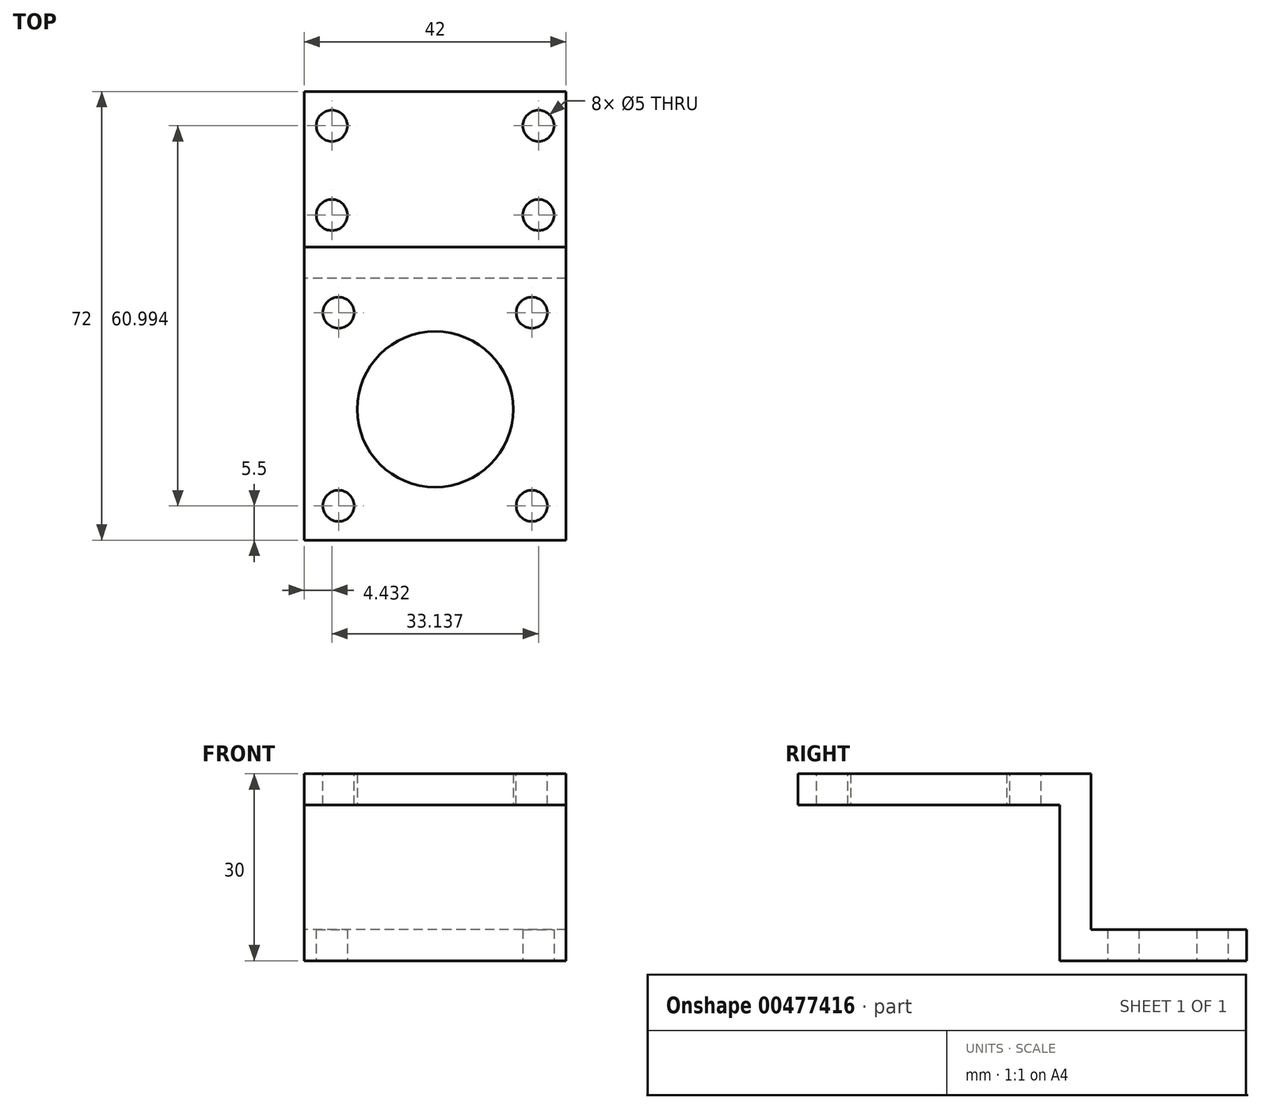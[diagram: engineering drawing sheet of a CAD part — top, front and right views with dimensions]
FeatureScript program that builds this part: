
annotation { "Feature Type Name" : "Feature", "Feature Type Description" : "" }
export const myFeature = defineFeature(function(context is Context, id is Id, definition is map)
    precondition{}
    {
        {
            var Q0;
            Q0=qCreatedBy(makeId("Top.planeOp"),FACE);
            var sketch = newSketch(context, id + "F0", { "sketchPlane" : qUnion([Q0])});
            skLineSegment(sketch, "E0.bottom", {"start": v(21, -21) * mm, "end": v(-21, -21) * mm});
            skLineSegment(sketch, "E0.top", {"start": v(21, 21) * mm, "end": v(-21, 21) * mm});
            skLineSegment(sketch, "E0.left", {"start": v(21, -21) * mm, "end": v(21, 21) * mm});
            skLineSegment(sketch, "E0.right", {"start": v(-21, -21) * mm, "end": v(-21, 21) * mm});
            skPoint(sketch, "E0.middle", {"position": v(0, 0) * mm});
            skSolve(sketch);
        }
        {
            var Q0;
            Q0=makeQuery(id+"F0.imprint","IMPRINT",FACE,{"disambiguationData":[TD([[makeQuery(id+"F0.imprint","IMPRINT",EDGE,{"derivedFrom":sQuery(id+"F0.wireOp",EDGE,"E0.bottom")}),-1.0]])]});
            extrude(context, id + "F1", {"entities" : qUnion([Q0]), "depth" : 5 * mm});
        }
        {
            var Q0;
            Q0=makeQuery(id+"F1.opExtrude","CAP_FACE",FACE,{"disambiguationData":[OSD([sQuery(id+"F0.wireOp",EDGE,"E0.bottom"),sQuery(id+"F0.wireOp",EDGE,"E0.top"),sQuery(id+"F0.wireOp",EDGE,"E0.left"),sQuery(id+"F0.wireOp",EDGE,"E0.right")])],"isStart":false});
            var sketch = newSketch(context, id + "F2", { "sketchPlane" : qUnion([Q0])});
            skLineSegment(sketch, "E1.bottom", {"start": v(15.5, -15.5) * mm, "end": v(-15.5, -15.5) * mm});
            skLineSegment(sketch, "E1.top", {"start": v(15.5, 15.5) * mm, "end": v(-15.5, 15.5) * mm});
            skLineSegment(sketch, "E1.left", {"start": v(15.5, -15.5) * mm, "end": v(15.5, 15.5) * mm});
            skLineSegment(sketch, "E1.right", {"start": v(-15.5, -15.5) * mm, "end": v(-15.5, 15.5) * mm});
            skPoint(sketch, "E1.middle", {"position": v(0, 0) * mm});
            skSolve(sketch);
        }
        {
            var Q0;
            Q0=sQuery(id+"F2.wireOp",VERTEX,"E1.top.end");
            var Q1;
            Q1=sQuery(id+"F2.wireOp",VERTEX,"E1.left.end");
            var Q2;
            Q2=sQuery(id+"F2.wireOp",VERTEX,"E1.left.start");
            var Q3;
            Q3=sQuery(id+"F2.wireOp",VERTEX,"E1.right.start");
            var Q4;
            Q4=makeQuery(id+"F1.opExtrude","SWEPT_BODY",BODY,{"disambiguationData":[OSD([sQuery(id+"F0.wireOp",EDGE,"E0.bottom"),sQuery(id+"F0.wireOp",EDGE,"E0.top"),sQuery(id+"F0.wireOp",EDGE,"E0.left"),sQuery(id+"F0.wireOp",EDGE,"E0.right")])]});
            hole(context, id + "F3", {"style" : HoleStyle.SIMPLE, "endStyle" : HoleEndStyle.THROUGH, "holeDiameter" : 5 * mm, "isTappedThrough" : true, "tappedDepth" : 12 * mm, "tapClearance" : 3, "locations" : qUnion([Q0, Q1, Q2, Q3]), "scope" : qUnion([Q4])});
        }
        {
            var Q0;
            Q0=makeQuery(id+"F1.opExtrude","SWEPT_FACE",FACE,{"disambiguationData":[OSD([sQuery(id+"F0.wireOp",EDGE,"E0.top")])]});
            var sketch = newSketch(context, id + "F4", { "sketchPlane" : qUnion([Q0])});
            skLineSegment(sketch, "E2.0.0", {"start": v(-21, 5) * mm, "end": v(-21, 5) * mm});
            skLineSegment(sketch, "E2.0.1", {"start": v(-21, 5) * mm, "end": v(21, 5) * mm});
            skLineSegment(sketch, "E2.0.2", {"start": v(21, 5) * mm, "end": v(21, 5) * mm});
            skLineSegment(sketch, "E2.0.3", {"start": v(21, 5) * mm, "end": v(-21, 5) * mm});
            skLineSegment(sketch, "E3.0.0", {"start": v(-21, 0) * mm, "end": v(21, 0) * mm});
            skLineSegment(sketch, "E4.0.1", {"start": v(21, 0) * mm, "end": v(21, 5) * mm});
            skLineSegment(sketch, "E4.0.3", {"start": v(-21, 5) * mm, "end": v(-21, 0) * mm});
            skSolve(sketch);
        }
        {
            var Q0;
            Q0=makeQuery(id+"F4.imprint","IMPRINT",FACE,{"disambiguationData":[TD([[makeQuery(id+"F4.imprint","IMPRINT",EDGE,{"derivedFrom":sQuery(id+"F4.wireOp",EDGE,"E3.0.0")}),1.0]])]});
            extrude(context, id + "F5", {"entities" : qUnion([Q0]), "operationType" : NewBodyOperationType.ADD, "depth" : 5 * mm});
        }
        {
            var Q0;
            Q0=makeQuery(id+"F5.boolean.opBoolean","MERGE",FACE,{"derivedFrom":[makeQuery(id+"F1.opExtrude","CAP_FACE",FACE,{"disambiguationData":[OSD([sQuery(id+"F0.wireOp",EDGE,"E0.bottom"),sQuery(id+"F0.wireOp",EDGE,"E0.top"),sQuery(id+"F0.wireOp",EDGE,"E0.left"),sQuery(id+"F0.wireOp",EDGE,"E0.right")])],"isStart":true}),makeQuery(id+"F5.opExtrude","SWEPT_FACE",FACE,{"disambiguationData":[OSD([sQuery(id+"F4.wireOp",EDGE,"E3.0.0")])]})]});
            var sketch = newSketch(context, id + "F6", { "sketchPlane" : qUnion([Q0])});
            skLineSegment(sketch, "E5.bottom", {"start": v(21, -26) * mm, "end": v(-21, -26) * mm});
            skLineSegment(sketch, "E5.top", {"start": v(21, -21) * mm, "end": v(-21, -21) * mm});
            skLineSegment(sketch, "E5.left", {"start": v(21, -26) * mm, "end": v(21, -21) * mm});
            skLineSegment(sketch, "E5.right", {"start": v(-21, -26) * mm, "end": v(-21, -21) * mm});
            skSolve(sketch);
        }
        {
            var Q0;
            Q0=makeQuery(id+"F6.imprint","IMPRINT",FACE,{"disambiguationData":[TD([[makeQuery(id+"F6.imprint","IMPRINT",EDGE,{"derivedFrom":sQuery(id+"F6.wireOp",EDGE,"E5.bottom")}),-1.0]])]});
            extrude(context, id + "F7", {"entities" : qUnion([Q0]), "operationType" : NewBodyOperationType.ADD, "depth" : 20 * mm});
        }
        {
            var Q0;
            Q0=makeQuery(id+"F7.opExtrude","CAP_FACE",FACE,{"disambiguationData":[OSD([sQuery(id+"F6.wireOp",EDGE,"E5.bottom"),sQuery(id+"F6.wireOp",EDGE,"E5.top"),sQuery(id+"F6.wireOp",EDGE,"E5.left"),sQuery(id+"F6.wireOp",EDGE,"E5.right")])],"isStart":false});
            var sketch = newSketch(context, id + "F8", { "sketchPlane" : qUnion([Q0])});
            skLineSegment(sketch, "E6.bottom", {"start": v(-21, -21) * mm, "end": v(21, -21) * mm});
            skLineSegment(sketch, "E6.top", {"start": v(-21, -51) * mm, "end": v(21, -51) * mm});
            skLineSegment(sketch, "E6.left", {"start": v(-21, -21) * mm, "end": v(-21, -51) * mm});
            skLineSegment(sketch, "E6.right", {"start": v(21, -21) * mm, "end": v(21, -51) * mm});
            skSolve(sketch);
        }
        {
            var Q0;
            {var subQ0=sQuery(id+"F8.wireOp",EDGE,"E6.bottom");Q0=makeQuery(id+"F8.imprint","IMPRINT",FACE,{"disambiguationData":[TD([[makeQuery(id+"F8.imprint","IMPRINT",EDGE,{"derivedFrom":subQ0}),1.0]])]});}
            var Q1;
            {var subQ0=sQuery(id+"F8.wireOp",EDGE,"E6.top");Q1=makeQuery(id+"F8.imprint","IMPRINT",FACE,{"disambiguationData":[TD([[makeQuery(id+"F8.imprint","IMPRINT",EDGE,{"derivedFrom":subQ0}),1.0]])]});}
            extrude(context, id + "F9", {"entities" : qUnion([Q0, Q1]), "operationType" : NewBodyOperationType.ADD, "depth" : 5 * mm});
        }
        {
            var Q0;
            Q0=makeQuery(id+"F9.opExtrude","CAP_FACE",FACE,{"disambiguationData":[OSD([sQuery(id+"F8.wireOp",EDGE,"E6.bottom"),sQuery(id+"F8.wireOp",EDGE,"E6.top"),sQuery(id+"F8.wireOp",EDGE,"E6.left"),sQuery(id+"F8.wireOp",EDGE,"E6.right")])],"isStart":false});
            var sketch = newSketch(context, id + "F10", { "sketchPlane" : qUnion([Q0])});
            skLineSegment(sketch, "E7.bottom", {"start": v(16.57, -45.5) * mm, "end": v(-16.57, -45.5) * mm});
            skLineSegment(sketch, "E7.top", {"start": v(16.57, -31.18) * mm, "end": v(-16.57, -31.18) * mm});
            skLineSegment(sketch, "E7.left", {"start": v(16.57, -45.5) * mm, "end": v(16.57, -31.18) * mm});
            skLineSegment(sketch, "E7.right", {"start": v(-16.57, -45.5) * mm, "end": v(-16.57, -31.18) * mm});
            skPoint(sketch, "E7.middle", {"position": v(0, -38.34) * mm});
            skSolve(sketch);
        }
        {
            var Q0;
            Q0=sQuery(id+"F10.wireOp",VERTEX,"E7.right.end");
            var Q1;
            Q1=sQuery(id+"F10.wireOp",VERTEX,"E7.left.end");
            var Q2;
            Q2=sQuery(id+"F10.wireOp",VERTEX,"E7.left.start");
            var Q3;
            Q3=sQuery(id+"F10.wireOp",VERTEX,"E7.bottom.end");
            var Q4;
            Q4=makeQuery(id+"F1.opExtrude","SWEPT_BODY",BODY,{"disambiguationData":[OSD([sQuery(id+"F0.wireOp",EDGE,"E0.bottom"),sQuery(id+"F0.wireOp",EDGE,"E0.top"),sQuery(id+"F0.wireOp",EDGE,"E0.left"),sQuery(id+"F0.wireOp",EDGE,"E0.right")])]});
            hole(context, id + "F11", {"style" : HoleStyle.SIMPLE, "endStyle" : HoleEndStyle.THROUGH, "holeDiameter" : 5 * mm, "isTappedThrough" : true, "tappedDepth" : 12 * mm, "tapClearance" : 3, "locations" : qUnion([Q0, Q1, Q2, Q3]), "scope" : qUnion([Q4])});
        }
        {
            var Q0;
            Q0=makeQuery(id+"F5.boolean.opBoolean","MERGE",FACE,{"derivedFrom":[makeQuery(id+"F1.opExtrude","CAP_FACE",FACE,{"disambiguationData":[OSD([sQuery(id+"F0.wireOp",EDGE,"E0.bottom"),sQuery(id+"F0.wireOp",EDGE,"E0.top"),sQuery(id+"F0.wireOp",EDGE,"E0.left"),sQuery(id+"F0.wireOp",EDGE,"E0.right")])],"isStart":true}),makeQuery(id+"F5.opExtrude","SWEPT_FACE",FACE,{"disambiguationData":[OSD([sQuery(id+"F4.wireOp",EDGE,"E3.0.0")])]})]});
            var sketch = newSketch(context, id + "F12", { "sketchPlane" : qUnion([Q0])});
            skCircle(sketch, "E8", {"center": v(0, 0) * mm, "radius": 7.5 * mm});
            skSolve(sketch);
        }
        {
            var Q0;
            Q0=sQuery(id+"F12.wireOp",VERTEX,"E8.center");
            var Q1;
            Q1=makeQuery(id+"F1.opExtrude","SWEPT_BODY",BODY,{"disambiguationData":[OSD([sQuery(id+"F0.wireOp",EDGE,"E0.bottom"),sQuery(id+"F0.wireOp",EDGE,"E0.top"),sQuery(id+"F0.wireOp",EDGE,"E0.left"),sQuery(id+"F0.wireOp",EDGE,"E0.right")])]});
            hole(context, id + "F13", {"style" : HoleStyle.SIMPLE, "endStyle" : HoleEndStyle.THROUGH, "holeDiameter" : 25 * mm, "isTappedThrough" : true, "tappedDepth" : 12 * mm, "tapClearance" : 3, "locations" : qUnion([Q0]), "scope" : qUnion([Q1])});
        }
    });
